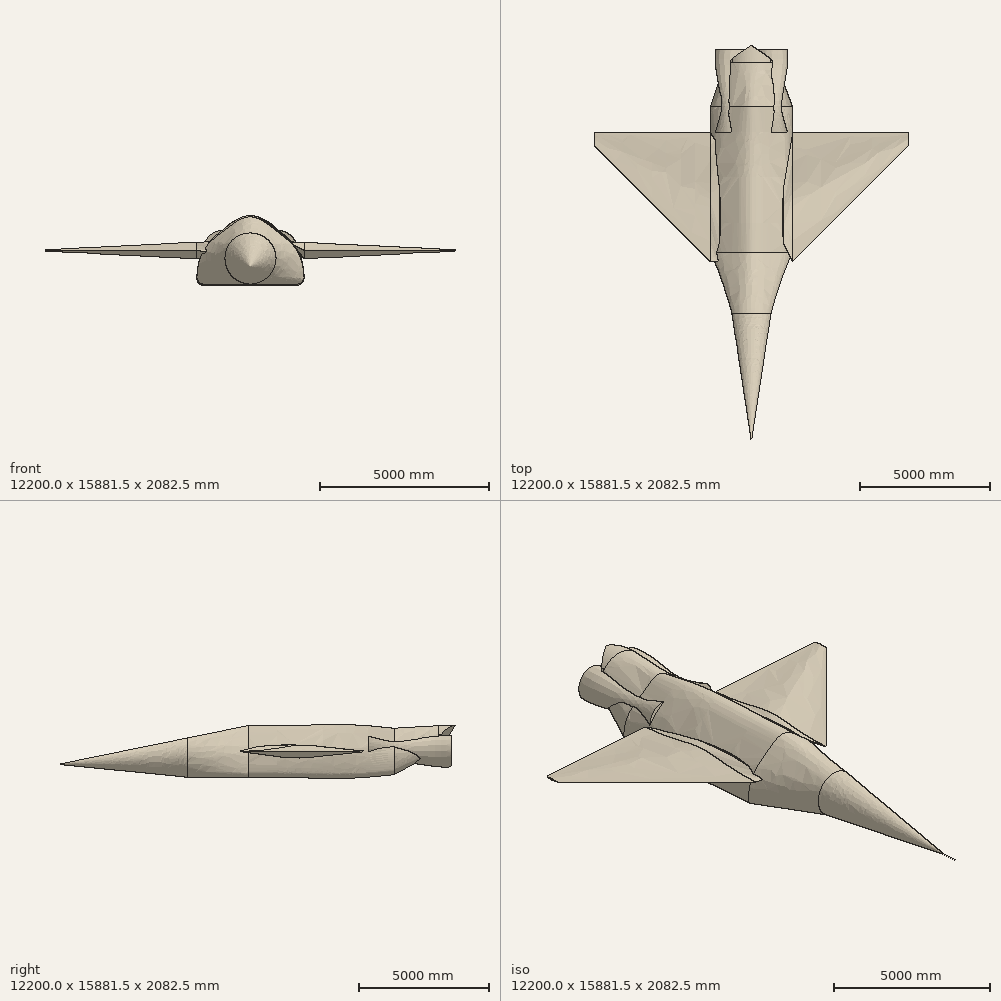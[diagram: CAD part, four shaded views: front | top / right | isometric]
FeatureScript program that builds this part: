
annotation { "Feature Type Name" : "Feature", "Feature Type Description" : "" }
export const myFeature = defineFeature(function(context is Context, id is Id, definition is map)
    precondition{}
    {
        {
            var Q0;
            Q0=qCreatedBy(makeId("Right.planeOp"),FACE);
            var sketch = newSketch(context, id + "F0", { "sketchPlane" : qUnion([Q0])});
            skLineSegment(sketch, "E0", {"start": v(0, 0) * mm, "end": v(-1750, 0) * mm});
            skLineSegment(sketch, "E1", {"start": v(-1750, 0) * mm, "end": v(-3500, 0) * mm});
            skLineSegment(sketch, "E2", {"start": v(-3500, 0) * mm, "end": v(-3500, -1000) * mm});
            skLineSegment(sketch, "E3", {"start": v(-3500, -1000) * mm, "end": v(-8500, -1000) * mm});
            skLineSegment(sketch, "E4", {"start": v(-8500, -1000) * mm, "end": v(-8500, -499.31) * mm});
            skLineSegment(sketch, "E5", {"start": v(-1151.4, 0) * mm, "end": v(-1151.4, 1000) * mm});
            skLineSegment(sketch, "E6", {"start": v(-1151.4, 1000) * mm, "end": v(-8500, -499.31) * mm});
            skLineSegment(sketch, "E7", {"start": v(-8500, -499.31) * mm, "end": v(-3500, -1000) * mm});
            skLineSegment(sketch, "E8", {"start": v(-3500, 0) * mm, "end": v(-3500, 520.82) * mm});
            skLineSegment(sketch, "E9", {"start": v(-8500, -499.31) * mm, "end": v(-8450, -499.31) * mm});
            skLineSegment(sketch, "E10", {"start": v(-8450, -499.31) * mm, "end": v(-8450, -489.1) * mm});
            skLineSegment(sketch, "E11", {"start": v(-8450, -499.31) * mm, "end": v(-8450, -504.32) * mm});
            skSolve(sketch);
        }
        {
            var Q0;
            Q0=sQuery(id+"F0.wireOp",EDGE,"E5");
            cPlane(context, id + "F1", {"entities" : qUnion([Q0]), "cplaneType" : CPlaneType.LINE_ANGLE, "offset" : 25 * mm, "angle" : 90 * degree, "oppositeDirection" : true, "width" : 150 * mm, "height" : 150 * mm});
        }
        {
            var Q0;
            Q0=qCreatedBy(id+"F1.planeOp",FACE);
            var sketch = newSketch(context, id + "F2", { "sketchPlane" : qUnion([Q0])});
            skLineSegment(sketch, "E12.top", {"start": v(-1394.2, -1000) * mm, "end": v(1394.2, -1000) * mm});
            skPoint(sketch, "E12.middle", {"position": v(0, 0) * mm});
            skFitSpline(sketch, "E13", {"points": [v(-1600, -1000) * mm, v(-848, 530) * mm, v(0, 1000) * mm, v(848, 530) * mm, v(1600, -1000) * mm], "startDerivative": vector(0, 10524.75) * mm, "endDerivative": vector(0, -10524.75) * mm});
            skArc(sketch, "E14", {"start": v(-735.27, 618.52) * mm, "mid": v(-1273.27, 435.52) * mm, "end": v(-1440.68, -107.53) * mm});
            skArc(sketch, "E15", {"start": v(1440.68, -107.53) * mm, "mid": v(1273.27, 435.52) * mm, "end": v(735.27, 618.52) * mm});
            skFitSpline(sketch, "E16.trimOffspring", {"points": [v(-1600, -1000) * mm, v(-848, 530) * mm, v(0, 1000) * mm, v(848, 530) * mm, v(1600, -1000) * mm], "startDerivative": vector(0, 10524.75) * mm, "endDerivative": vector(0, -10524.75) * mm});
            skFitSpline(sketch, "E17.trimOffspring", {"points": [v(-1600, -1000) * mm, v(-848, 530) * mm, v(0, 1000) * mm, v(848, 530) * mm, v(1600, -1000) * mm], "startDerivative": vector(0, 10524.75) * mm, "endDerivative": vector(0, -10524.75) * mm});
            skArc(sketch, "E18.filletArc", {"start": v(-1593.82, -787.83) * mm, "mid": v(-1539.85, -937.05) * mm, "end": v(-1394.2, -1000) * mm});
            skArc(sketch, "E19.filletArc", {"start": v(1394.2, -1000) * mm, "mid": v(1539.85, -937.05) * mm, "end": v(1593.82, -787.83) * mm});
            skSolve(sketch);
        }
        {
            var Q0;
            Q0=qCreatedBy(makeId("Front.planeOp"),FACE);
            var sketch = newSketch(context, id + "F3", { "sketchPlane" : qUnion([Q0])});
            skLineSegment(sketch, "E20.top", {"start": v(-1394.2, -1000) * mm, "end": v(1394.2, -1000) * mm});
            skPoint(sketch, "E20.middle", {"position": v(0, 0) * mm});
            skFitSpline(sketch, "E21", {"points": [v(-1600, -1000) * mm, v(-848, 530) * mm, v(0, 1000) * mm, v(848, 530) * mm, v(1600, -1000) * mm], "startDerivative": vector(0, 10524.75) * mm, "endDerivative": vector(0, -10524.75) * mm});
            skArc(sketch, "E22", {"start": v(-735.27, 618.52) * mm, "mid": v(-1273.27, 435.52) * mm, "end": v(-1440.68, -107.53) * mm});
            skArc(sketch, "E23", {"start": v(1440.68, -107.53) * mm, "mid": v(1273.27, 435.52) * mm, "end": v(735.27, 618.52) * mm});
            skFitSpline(sketch, "E24.trimOffspring", {"points": [v(-1600, -1000) * mm, v(-848, 530) * mm, v(0, 1000) * mm, v(848, 530) * mm, v(1600, -1000) * mm], "startDerivative": vector(0, 10524.75) * mm, "endDerivative": vector(0, -10524.75) * mm});
            skFitSpline(sketch, "E25.trimOffspring", {"points": [v(-1600, -1000) * mm, v(-848, 530) * mm, v(0, 1000) * mm, v(848, 530) * mm, v(1600, -1000) * mm], "startDerivative": vector(0, 10524.75) * mm, "endDerivative": vector(0, -10524.75) * mm});
            skArc(sketch, "E26.filletArc", {"start": v(-1593.82, -787.83) * mm, "mid": v(-1539.85, -937.05) * mm, "end": v(-1394.2, -1000) * mm});
            skArc(sketch, "E27.filletArc", {"start": v(1394.2, -1000) * mm, "mid": v(1539.85, -937.05) * mm, "end": v(1593.82, -787.83) * mm});
            skSolve(sketch);
        }
        {
            var Q0;
            Q0=qCreatedBy(makeId("Front.planeOp"),FACE);
            cPlane(context, id + "F4", {"entities" : qUnion([Q0]), "cplaneType" : CPlaneType.OFFSET, "offset" : 3500 * mm, "oppositeDirection" : true, "width" : 150 * mm, "height" : 150 * mm});
        }
        {
            var Q0;
            Q0=qCreatedBy(id+"F4.planeOp",FACE);
            var sketch = newSketch(context, id + "F5", { "sketchPlane" : qUnion([Q0])});
            skLineSegment(sketch, "E28.top", {"start": v(-1394.2, -1000) * mm, "end": v(1394.2, -1000) * mm});
            skPoint(sketch, "E28.middle", {"position": v(0, 0) * mm});
            skFitSpline(sketch, "E29", {"points": [v(-1600, -1000) * mm, v(-848, 530) * mm, v(0, 1000) * mm, v(848, 530) * mm, v(1600, -1000) * mm], "startDerivative": vector(0, 10524.75) * mm, "endDerivative": vector(0, -10524.75) * mm});
            skArc(sketch, "E30", {"start": v(-735.27, 618.52) * mm, "mid": v(-1273.27, 435.52) * mm, "end": v(-1440.68, -107.53) * mm});
            skArc(sketch, "E31", {"start": v(1440.68, -107.53) * mm, "mid": v(1273.27, 435.52) * mm, "end": v(735.27, 618.52) * mm});
            skFitSpline(sketch, "E32.trimOffspring", {"points": [v(-1600, -1000) * mm, v(-848, 530) * mm, v(0, 1000) * mm, v(848, 530) * mm, v(1600, -1000) * mm], "startDerivative": vector(0, 10524.75) * mm, "endDerivative": vector(0, -10524.75) * mm});
            skFitSpline(sketch, "E33.trimOffspring", {"points": [v(-1600, -1000) * mm, v(-848, 530) * mm, v(0, 1000) * mm, v(848, 530) * mm, v(1600, -1000) * mm], "startDerivative": vector(0, 10524.75) * mm, "endDerivative": vector(0, -10524.75) * mm});
            skArc(sketch, "E34.filletArc", {"start": v(-1593.82, -787.83) * mm, "mid": v(-1539.85, -937.05) * mm, "end": v(-1394.2, -1000) * mm});
            skArc(sketch, "E35.filletArc", {"start": v(1394.2, -1000) * mm, "mid": v(1539.85, -937.05) * mm, "end": v(1593.82, -787.83) * mm});
            skSolve(sketch);
        }
        {
            var Q0;
            Q0=qCreatedBy(makeId("Front.planeOp"),FACE);
            cPlane(context, id + "F6", {"entities" : qUnion([Q0]), "cplaneType" : CPlaneType.OFFSET, "offset" : 4500 * mm, "oppositeDirection" : true, "width" : 150 * mm, "height" : 150 * mm});
        }
        {
            var Q0;
            Q0=qCreatedBy(id+"F6.planeOp",FACE);
            var sketch = newSketch(context, id + "F7", { "sketchPlane" : qUnion([Q0])});
            skLineSegment(sketch, "E36.top", {"start": v(-1413.07, -900) * mm, "end": v(1413.07, -900) * mm});
            skPoint(sketch, "E36.middle", {"position": v(0, 0) * mm});
            skFitSpline(sketch, "E37", {"points": [v(-1600, -900) * mm, v(-784.42, 441.24) * mm, v(0, 900) * mm, v(784.42, 441.24) * mm, v(1600, -900) * mm], "startDerivative": vector(0, 9508.62) * mm, "endDerivative": vector(0, -9508.62) * mm});
            skArc(sketch, "E38", {"start": v(-719.25, 488.69) * mm, "mid": v(-1131.76, 394.84) * mm, "end": v(-1324.66, 18.33) * mm});
            skArc(sketch, "E39", {"start": v(1324.66, 18.33) * mm, "mid": v(1131.76, 394.84) * mm, "end": v(719.25, 488.69) * mm});
            skFitSpline(sketch, "E40.trimOffspring", {"points": [v(-1600, -900) * mm, v(-784.42, 441.24) * mm, v(0, 900) * mm, v(784.42, 441.24) * mm, v(1600, -900) * mm], "startDerivative": vector(0, 9508.62) * mm, "endDerivative": vector(0, -9508.62) * mm});
            skFitSpline(sketch, "E41.trimOffspring", {"points": [v(-1600, -900) * mm, v(-784.42, 441.24) * mm, v(0, 900) * mm, v(784.42, 441.24) * mm, v(1600, -900) * mm], "startDerivative": vector(0, 9508.62) * mm, "endDerivative": vector(0, -9508.62) * mm});
            skArc(sketch, "E42.filletArc", {"start": v(-1592.48, -705.43) * mm, "mid": v(-1545.4, -842.02) * mm, "end": v(-1413.07, -900) * mm});
            skArc(sketch, "E43.filletArc", {"start": v(1413.07, -900) * mm, "mid": v(1545.4, -842.02) * mm, "end": v(1592.48, -705.43) * mm});
            skLineSegment(sketch, "E44", {"start": v(-719.25, 488.69) * mm, "end": v(-1324.66, 18.33) * mm, "construction": true});
            skLineSegment(sketch, "E45", {"start": v(719.25, 488.69) * mm, "end": v(1324.66, 18.33) * mm, "construction": true});
            skSolve(sketch);
        }
        {
            var Q0;
            Q0=qCreatedBy(makeId("Front.planeOp"),FACE);
            cPlane(context, id + "F8", {"entities" : qUnion([Q0]), "cplaneType" : CPlaneType.OFFSET, "offset" : 6232.05 * mm, "oppositeDirection" : true, "width" : 150 * mm, "height" : 150 * mm});
        }
        {
            var Q0;
            Q0=qCreatedBy(id+"F8.planeOp",FACE);
            var sketch = newSketch(context, id + "F9", { "sketchPlane" : qUnion([Q0])});
            skArc(sketch, "E46", {"start": v(998.61, 52.63) * mm, "mid": v(0, 1000) * mm, "end": v(-998.61, 52.63) * mm});
            skLineSegment(sketch, "E47", {"start": v(0, 0) * mm, "end": v(-948.68, 0) * mm});
            skLineSegment(sketch, "E48", {"start": v(0, 0) * mm, "end": v(948.68, 0) * mm});
            skLineSegment(sketch, "E49", {"start": v(0, 1000) * mm, "end": v(0, 675) * mm, "construction": true});
            skLineSegment(sketch, "E50", {"start": v(0, 675) * mm, "end": v(-737.82, 675) * mm, "construction": true});
            skLineSegment(sketch, "E51", {"start": v(0, 675) * mm, "end": v(737.82, 675) * mm, "construction": true});
            skPoint(sketch, "E52.visualSharp", {"position": v(-1000, 0) * mm});
            skArc(sketch, "E52.filletArc", {"start": v(-998.61, 52.63) * mm, "mid": v(-984.96, 15.59) * mm, "end": v(-948.68, 0) * mm});
            skPoint(sketch, "E53.visualSharp", {"position": v(1000, 0) * mm});
            skArc(sketch, "E53.filletArc", {"start": v(948.68, 0) * mm, "mid": v(984.96, 15.59) * mm, "end": v(998.61, 52.63) * mm});
            skSolve(sketch);
        }
        {
            var Q0;
            Q0=makeQuery(id+"F2.imprint","IMPRINT",FACE,{"disambiguationData":[TD([[makeQuery(id+"F2.imprint","IMPRINT",EDGE,{"derivedFrom":sQuery(id+"F2.wireOp",EDGE,"E12.top")}),1.0]])]});
            var Q1;
            Q1=makeQuery(id+"F3.imprint","IMPRINT",FACE,{"disambiguationData":[TD([[makeQuery(id+"F3.imprint","IMPRINT",EDGE,{"derivedFrom":sQuery(id+"F3.wireOp",EDGE,"E20.top")}),1.0]])]});
            var Q2;
            Q2=makeQuery(id+"F5.imprint","IMPRINT",FACE,{"disambiguationData":[TD([[makeQuery(id+"F5.imprint","IMPRINT",EDGE,{"derivedFrom":sQuery(id+"F5.wireOp",EDGE,"E28.top")}),1.0]])]});
            var Q3;
            Q3=makeQuery(id+"F7.imprint","IMPRINT",FACE,{"disambiguationData":[TD([[makeQuery(id+"F7.imprint","IMPRINT",EDGE,{"derivedFrom":sQuery(id+"F7.wireOp",EDGE,"E36.top")}),1.0]])]});
            loft(context, id + "F10", {"sheetProfilesArray" : [{ "sheetProfileEntities" : qUnion([Q0]) }, { "sheetProfileEntities" : qUnion([Q1]) }, { "sheetProfileEntities" : qUnion([Q2]) }, { "sheetProfileEntities" : qUnion([Q3]) }]});
        }
        {
            var Q0;
            Q0=sQuery(id+"F7.wireOp",EDGE,"E44");
            var Q1;
            Q1=sQuery(id+"F9.wireOp",VERTEX,"E50.end");
            cPlane(context, id + "F11", {"entities" : qUnion([Q0, Q1]), "cplaneType" : CPlaneType.LINE_ANGLE, "offset" : 25 * mm, "angle" : 180 * degree, "width" : 150 * mm, "height" : 150 * mm});
        }
        {
            var Q0;
            Q0=qCreatedBy(id+"F11.planeOp",FACE);
            var sketch = newSketch(context, id + "F12", { "sketchPlane" : qUnion([Q0])});
            skLineSegment(sketch, "E54", {"start": v(-589.34, 4526.34) * mm, "end": v(-612.8, 6268.32) * mm});
            skLineSegment(sketch, "E55", {"start": v(-1354.08, 4472.19) * mm, "end": v(-612.8, 6268.32) * mm});
            skSolve(sketch);
        }
        {
            var Q0;
            Q0=sQuery(id+"F7.wireOp",EDGE,"E45");
            var Q1;
            Q1=sQuery(id+"F9.wireOp",VERTEX,"E51.end");
            cPlane(context, id + "F13", {"entities" : qUnion([Q0, Q1]), "cplaneType" : CPlaneType.LINE_ANGLE, "offset" : 25 * mm, "angle" : 0 * degree, "width" : 150 * mm, "height" : 150 * mm});
        }
        {
            var Q0;
            Q0=qCreatedBy(id+"F13.planeOp",FACE);
            var sketch = newSketch(context, id + "F14", { "sketchPlane" : qUnion([Q0])});
            skLineSegment(sketch, "E56", {"start": v(589.34, 4526.34) * mm, "end": v(612.8, 6268.32) * mm});
            skLineSegment(sketch, "E57", {"start": v(1354.08, 4472.19) * mm, "end": v(612.8, 6268.32) * mm});
            skSolve(sketch);
        }
        {
            var Q1;
            Q1=makeQuery(id+"F10.opLoft","CAP_FACE",FACE,{"disambiguationData":[OSD([makeQuery(id+"F7.imprint","IMPRINT",FACE,{"disambiguationData":[TD([[makeQuery(id+"F7.imprint","IMPRINT",EDGE,{"derivedFrom":sQuery(id+"F7.wireOp",EDGE,"E36.top")}),1.0]])]})])],"isStart":true});
            var Q2;
            Q2=makeQuery(id+"F9.imprint","IMPRINT",FACE,{"disambiguationData":[TD([[makeQuery(id+"F9.imprint","IMPRINT",EDGE,{"derivedFrom":sQuery(id+"F9.wireOp",EDGE,"E46")}),1.0]])]});
            var Q3;
            Q3=sQuery(id+"F12.wireOp",EDGE,"E54");
            var Q4;
            Q4=sQuery(id+"F14.wireOp",EDGE,"E56");
            loft(context, id + "F15", {"operationType" : NewBodyOperationType.ADD, "addGuides" : true, "sheetProfilesArray" : [{ "sheetProfileEntities" : qUnion([Q1]) }, { "sheetProfileEntities" : qUnion([Q2]) }], "guidesArray" : [{ "guideEntities" : qUnion([Q3]), "guideDerivativeType" : LoftGuideDerivativeType.DEFAULT, "guideDerivativeMagnitude" : 1 }, { "guideEntities" : qUnion([Q4]), "guideDerivativeType" : LoftGuideDerivativeType.DEFAULT, "guideDerivativeMagnitude" : 1 }]});
        }
        {
            var Q0;
            Q0=makeQuery(id+"F15.opLoft","CAP_FACE",FACE,{"disambiguationData":[OSD([makeQuery(id+"F9.imprint","IMPRINT",FACE,{"disambiguationData":[TD([[makeQuery(id+"F9.imprint","IMPRINT",EDGE,{"derivedFrom":sQuery(id+"F9.wireOp",EDGE,"E46")}),1.0]])]})])],"isStart":true});
            extrude(context, id + "F16", {"entities" : qUnion([Q0]), "operationType" : NewBodyOperationType.ADD, "depth" : 649.4 * mm, "offsetDistance" : 25 * mm});
        }
        {
            var Q0;
            Q0=qCreatedBy(makeId("Right.planeOp"),FACE);
            var sketch = newSketch(context, id + "F17", { "sketchPlane" : qUnion([Q0])});
            skLineSegment(sketch, "E58", {"start": v(0, 0) * mm, "end": v(4500, 0) * mm});
            skLineSegment(sketch, "E59", {"start": v(4500, 0) * mm, "end": v(6232.05, 0) * mm});
            skLineSegment(sketch, "E60", {"start": v(4500, 0) * mm, "end": v(4500, 1000) * mm});
            skLineSegment(sketch, "E61", {"start": v(4500, 1000) * mm, "end": v(6881.46, 1000) * mm});
            skLineSegment(sketch, "E62", {"start": v(6881.46, 1000) * mm, "end": v(6881.46, -1000) * mm});
            skLineSegment(sketch, "E63", {"start": v(6881.46, 1000) * mm, "end": v(6232.05, 0) * mm});
            skLineSegment(sketch, "E64", {"start": v(6232.05, 0) * mm, "end": v(5582.64, -1000) * mm});
            skLineSegment(sketch, "E65", {"start": v(5582.64, -1000) * mm, "end": v(6881.46, -1000) * mm});
            skSolve(sketch);
        }
        {
            var Q0;
            Q0=makeQuery(id+"F17.imprint","IMPRINT",FACE,{"disambiguationData":[TD([[makeQuery(id+"F17.imprint","IMPRINT",EDGE,{"derivedFrom":sQuery(id+"F17.wireOp",EDGE,"E62")}),-1.0]])]});
            var Q1;
            Q1=sQuery(id+"F17.wireOp",EDGE,"E61");
            revolve(context, id + "F18", {"operationType" : NewBodyOperationType.REMOVE, "entities" : qUnion([Q0]), "axis" : qUnion([Q1]), "revolveType" : RevolveType.SYMMETRIC, "oppositeDirection" : true, "angle" : 182 * degree});
        }
        {
            var Q0;
            Q0=qCreatedBy(id+"F1.planeOp",FACE);
            var sketch = newSketch(context, id + "F19", { "sketchPlane" : qUnion([Q0])});
            skLineSegment(sketch, "E66.top", {"start": v(-1394.2, -1000) * mm, "end": v(1394.2, -1000) * mm});
            skPoint(sketch, "E66.middle", {"position": v(0, 0) * mm});
            skFitSpline(sketch, "E67", {"points": [v(-1600, -1000) * mm, v(-848, 530) * mm, v(0, 1000) * mm, v(848, 530) * mm, v(1600, -1000) * mm], "startDerivative": vector(0, 10524.75) * mm, "endDerivative": vector(0, -10524.75) * mm});
            skArc(sketch, "E68.filletArc", {"start": v(-1593.82, -787.83) * mm, "mid": v(-1539.85, -937.05) * mm, "end": v(-1394.2, -1000) * mm});
            skArc(sketch, "E69.filletArc", {"start": v(1394.2, -1000) * mm, "mid": v(1539.85, -937.05) * mm, "end": v(1593.82, -787.83) * mm});
            skLineSegment(sketch, "E70", {"start": v(-1593.82, -787.83) * mm, "end": v(-1394.2, -1000) * mm, "construction": true});
            skLineSegment(sketch, "E71", {"start": v(1593.82, -787.83) * mm, "end": v(1394.2, -1000) * mm, "construction": true});
            skSolve(sketch);
        }
        {
            var Q0;
            Q0=qCreatedBy(makeId("Front.planeOp"),FACE);
            cPlane(context, id + "F20", {"entities" : qUnion([Q0]), "cplaneType" : CPlaneType.OFFSET, "offset" : 3500 * mm, "width" : 150 * mm, "height" : 150 * mm});
        }
        {
            var Q0;
            Q0=qCreatedBy(id+"F20.planeOp",FACE);
            var sketch = newSketch(context, id + "F21", { "sketchPlane" : qUnion([Q0])});
            skCircle(sketch, "E72", {"center": v(0, -239.59) * mm, "radius": 760.41 * mm});
            skLineSegment(sketch, "E73", {"start": v(0, -1000) * mm, "end": v(0, -800) * mm, "construction": true});
            skLineSegment(sketch, "E74", {"start": v(0, -800) * mm, "end": v(-513.97, -800) * mm, "construction": true});
            skLineSegment(sketch, "E75", {"start": v(0, -800) * mm, "end": v(513.97, -800) * mm, "construction": true});
            skSolve(sketch);
        }
        {
            var Q0;
            Q0=qCreatedBy(makeId("Front.planeOp"),FACE);
            cPlane(context, id + "F22", {"entities" : qUnion([Q0]), "cplaneType" : CPlaneType.OFFSET, "offset" : 8450 * mm, "width" : 150 * mm, "height" : 150 * mm});
        }
        {
            var Q0;
            Q0=qCreatedBy(id+"F22.planeOp",FACE);
            var sketch = newSketch(context, id + "F23", { "sketchPlane" : qUnion([Q0])});
            skCircle(sketch, "E76", {"center": v(0, -496.71) * mm, "radius": 7.6 * mm});
            skSolve(sketch);
        }
        {
            var Q0;
            Q0=sQuery(id+"F19.wireOp",EDGE,"E70");
            var Q1;
            Q1=sQuery(id+"F21.wireOp",VERTEX,"E74.end");
            cPlane(context, id + "F24", {"entities" : qUnion([Q0, Q1]), "cplaneType" : CPlaneType.LINE_ANGLE, "offset" : 25 * mm, "angle" : 0 * degree, "width" : 150 * mm, "height" : 150 * mm});
        }
        {
            var Q0;
            Q0=qCreatedBy(id+"F24.planeOp",FACE);
            var sketch = newSketch(context, id + "F25", { "sketchPlane" : qUnion([Q0])});
            skLineSegment(sketch, "E77", {"start": v(3032.27, -230.44) * mm, "end": v(558.11, 518.4) * mm});
            skLineSegment(sketch, "E78", {"start": v(3032.27, -230.44) * mm, "end": v(558.11, 227.09) * mm});
            skSolve(sketch);
        }
        {
            var Q0;
            Q0=sQuery(id+"F19.wireOp",EDGE,"E71");
            var Q1;
            Q1=sQuery(id+"F21.wireOp",VERTEX,"E75.end");
            cPlane(context, id + "F26", {"entities" : qUnion([Q0, Q1]), "cplaneType" : CPlaneType.LINE_ANGLE, "offset" : 25 * mm, "angle" : 180 * degree, "width" : 150 * mm, "height" : 150 * mm});
        }
        {
            var Q0;
            Q0=qCreatedBy(id+"F26.planeOp",FACE);
            var sketch = newSketch(context, id + "F27", { "sketchPlane" : qUnion([Q0])});
            skLineSegment(sketch, "E79", {"start": v(-3032.27, -230.44) * mm, "end": v(-558.11, 518.4) * mm});
            skLineSegment(sketch, "E80", {"start": v(-3032.27, -230.44) * mm, "end": v(-558.11, 227.09) * mm});
            skSolve(sketch);
        }
        {
            var Q1;
            Q1=makeQuery(id+"F19.imprint","IMPRINT",FACE,{"disambiguationData":[TD([[makeQuery(id+"F19.imprint","IMPRINT",EDGE,{"derivedFrom":sQuery(id+"F19.wireOp",EDGE,"E66.top")}),1.0]])]});
            var Q2;
            Q2=makeQuery(id+"F21.imprint","IMPRINT",FACE,{"disambiguationData":[TD([[makeQuery(id+"F21.imprint","IMPRINT",EDGE,{"derivedFrom":sQuery(id+"F21.wireOp",EDGE,"E72")}),1.0]])]});
            var Q3;
            Q3=sQuery(id+"F25.wireOp",EDGE,"E77");
            var Q4;
            Q4=sQuery(id+"F27.wireOp",EDGE,"E79");
            loft(context, id + "F28", {"operationType" : NewBodyOperationType.ADD, "addGuides" : true, "sheetProfilesArray" : [{ "sheetProfileEntities" : qUnion([Q1]) }, { "sheetProfileEntities" : qUnion([Q2]) }], "guidesArray" : [{ "guideEntities" : qUnion([Q3]), "guideDerivativeType" : LoftGuideDerivativeType.DEFAULT, "guideDerivativeMagnitude" : 1 }, { "guideEntities" : qUnion([Q4]), "guideDerivativeType" : LoftGuideDerivativeType.DEFAULT, "guideDerivativeMagnitude" : 1 }]});
        }
        {
            var Q1;
            Q1=makeQuery(id+"F28.opLoft","CAP_FACE",FACE,{"disambiguationData":[OSD([makeQuery(id+"F21.imprint","IMPRINT",FACE,{"disambiguationData":[TD([[makeQuery(id+"F21.imprint","IMPRINT",EDGE,{"derivedFrom":sQuery(id+"F21.wireOp",EDGE,"E72")}),1.0]])]})])],"isStart":true});
            var Q2;
            Q2=makeQuery(id+"F23.imprint","IMPRINT",FACE,{"disambiguationData":[TD([[makeQuery(id+"F23.imprint","IMPRINT",EDGE,{"derivedFrom":sQuery(id+"F23.wireOp",EDGE,"E76")}),1.0]])]});
            loft(context, id + "F29", {"operationType" : NewBodyOperationType.ADD, "sheetProfilesArray" : [{ "sheetProfileEntities" : qUnion([Q1]) }, { "sheetProfileEntities" : qUnion([Q2]) }]});
        }
        {
            var Q0;
            Q0=makeQuery(id+"F29.opLoft","CAP_FACE",FACE,{"disambiguationData":[OSD([makeQuery(id+"F23.imprint","IMPRINT",FACE,{"disambiguationData":[TD([[makeQuery(id+"F23.imprint","IMPRINT",EDGE,{"derivedFrom":sQuery(id+"F23.wireOp",EDGE,"E76")}),1.0]])]})])],"isStart":true});
            extrude(context, id + "F30", {"entities" : qUnion([Q0]), "operationType" : NewBodyOperationType.ADD, "depth" : 550 * mm, "offsetDistance" : 25 * mm});
        }
        {
            var Q0;
            Q0=qCreatedBy(makeId("Front.planeOp"),FACE);
            cPlane(context, id + "F31", {"entities" : qUnion([Q0]), "cplaneType" : CPlaneType.OFFSET, "offset" : 3500 * mm, "oppositeDirection" : true, "width" : 150 * mm, "height" : 150 * mm});
        }
        {
            var Q0;
            Q0=qCreatedBy(id+"F31.planeOp",FACE);
            var sketch = newSketch(context, id + "F32", { "sketchPlane" : qUnion([Q0])});
            skCircle(sketch, "E81", {"center": v(-800, 0) * mm, "radius": 600 * mm});
            skCircle(sketch, "E82", {"center": v(800, 0) * mm, "radius": 600 * mm});
            skSolve(sketch);
        }
        {
            var Q0;
            Q0=qCreatedBy(makeId("Front.planeOp"),FACE);
            cPlane(context, id + "F33", {"entities" : qUnion([Q0]), "cplaneType" : CPlaneType.OFFSET, "offset" : 4500 * mm, "oppositeDirection" : true, "width" : 150 * mm, "height" : 150 * mm});
        }
        {
            var Q0;
            Q0=qCreatedBy(id+"F33.planeOp",FACE);
            var sketch = newSketch(context, id + "F34", { "sketchPlane" : qUnion([Q0])});
            skCircle(sketch, "E83", {"center": v(-800, 0) * mm, "radius": 400 * mm});
            skCircle(sketch, "E84", {"center": v(800, 0) * mm, "radius": 400 * mm});
            skSolve(sketch);
        }
        {
            var Q0;
            Q0=qCreatedBy(makeId("Front.planeOp"),FACE);
            cPlane(context, id + "F35", {"entities" : qUnion([Q0]), "cplaneType" : CPlaneType.OFFSET, "offset" : 6232.05 * mm, "oppositeDirection" : true, "width" : 150 * mm, "height" : 150 * mm});
        }
        {
            var Q0;
            Q0=qCreatedBy(id+"F35.planeOp",FACE);
            var sketch = newSketch(context, id + "F36", { "sketchPlane" : qUnion([Q0])});
            skCircle(sketch, "E85", {"center": v(-800, 0) * mm, "radius": 600 * mm});
            skCircle(sketch, "E86", {"center": v(800, 0) * mm, "radius": 600 * mm});
            skSolve(sketch);
        }
        {
            var Q0;
            Q0=qCreatedBy(makeId("Front.planeOp"),FACE);
            cPlane(context, id + "F37", {"entities" : qUnion([Q0]), "cplaneType" : CPlaneType.OFFSET, "offset" : 6732.05 * mm, "oppositeDirection" : true, "width" : 150 * mm, "height" : 150 * mm});
        }
        {
            var Q0;
            Q0=qCreatedBy(id+"F37.planeOp",FACE);
            var sketch = newSketch(context, id + "F38", { "sketchPlane" : qUnion([Q0])});
            skCircle(sketch, "E87", {"center": v(-800, 0) * mm, "radius": 600 * mm});
            skCircle(sketch, "E88", {"center": v(800, 0) * mm, "radius": 600 * mm});
            skSolve(sketch);
        }
        {
            var Q0;
            Q0=makeQuery(id+"F32.imprint","IMPRINT",FACE,{"disambiguationData":[TD([[makeQuery(id+"F32.imprint","IMPRINT",EDGE,{"derivedFrom":sQuery(id+"F32.wireOp",EDGE,"E81")}),1.0]])]});
            var Q1;
            Q1=makeQuery(id+"F34.imprint","IMPRINT",FACE,{"disambiguationData":[TD([[makeQuery(id+"F34.imprint","IMPRINT",EDGE,{"derivedFrom":sQuery(id+"F34.wireOp",EDGE,"E83")}),1.0]])]});
            var Q2;
            Q2=makeQuery(id+"F36.imprint","IMPRINT",FACE,{"disambiguationData":[TD([[makeQuery(id+"F36.imprint","IMPRINT",EDGE,{"derivedFrom":sQuery(id+"F36.wireOp",EDGE,"E85")}),1.0]])]});
            var Q3;
            Q3=makeQuery(id+"F38.imprint","IMPRINT",FACE,{"disambiguationData":[TD([[makeQuery(id+"F38.imprint","IMPRINT",EDGE,{"derivedFrom":sQuery(id+"F38.wireOp",EDGE,"E87")}),1.0]])]});
            loft(context, id + "F39", {"sheetProfilesArray" : [{ "sheetProfileEntities" : qUnion([Q0]) }, { "sheetProfileEntities" : qUnion([Q1]) }, { "sheetProfileEntities" : qUnion([Q2]) }, { "sheetProfileEntities" : qUnion([Q3]) }]});
        }
        {
            var Q0;
            Q0=makeQuery(id+"F32.imprint","IMPRINT",FACE,{"disambiguationData":[TD([[makeQuery(id+"F32.imprint","IMPRINT",EDGE,{"derivedFrom":sQuery(id+"F32.wireOp",EDGE,"E82")}),1.0]])]});
            var Q1;
            Q1=makeQuery(id+"F34.imprint","IMPRINT",FACE,{"disambiguationData":[TD([[makeQuery(id+"F34.imprint","IMPRINT",EDGE,{"derivedFrom":sQuery(id+"F34.wireOp",EDGE,"E84")}),1.0]])]});
            var Q2;
            Q2=makeQuery(id+"F36.imprint","IMPRINT",FACE,{"disambiguationData":[TD([[makeQuery(id+"F36.imprint","IMPRINT",EDGE,{"derivedFrom":sQuery(id+"F36.wireOp",EDGE,"E86")}),1.0]])]});
            var Q3;
            Q3=makeQuery(id+"F38.imprint","IMPRINT",FACE,{"disambiguationData":[TD([[makeQuery(id+"F38.imprint","IMPRINT",EDGE,{"derivedFrom":sQuery(id+"F38.wireOp",EDGE,"E88")}),1.0]])]});
            loft(context, id + "F40", {"sheetProfilesArray" : [{ "sheetProfileEntities" : qUnion([Q0]) }, { "sheetProfileEntities" : qUnion([Q1]) }, { "sheetProfileEntities" : qUnion([Q2]) }, { "sheetProfileEntities" : qUnion([Q3]) }]});
        }
        {
            var Q0;
            Q0=qCreatedBy(makeId("Right.planeOp"),FACE);
            var sketch = newSketch(context, id + "F41", { "sketchPlane" : qUnion([Q0])});
            skFitSpline(sketch, "E89", {"points": [v(-1500, -50) * mm, v(0, 250) * mm, v(3000, -50) * mm, v(0, -250) * mm, v(-1500, -50) * mm]});
            skSolve(sketch);
        }
        {
            var Q0;
            Q0=qCreatedBy(makeId("Right.planeOp"),FACE);
            cPlane(context, id + "F42", {"entities" : qUnion([Q0]), "cplaneType" : CPlaneType.OFFSET, "offset" : 1600 * mm, "oppositeDirection" : true, "width" : 150 * mm, "height" : 150 * mm});
        }
        {
            var Q0;
            Q0=qCreatedBy(id+"F42.planeOp",FACE);
            var sketch = newSketch(context, id + "F43", { "sketchPlane" : qUnion([Q0])});
            skFitSpline(sketch, "E90", {"points": [v(-1500, 0) * mm, v(1000, 250) * mm, v(3500, 0) * mm], "startDerivative": vector(7500, 0) * mm, "endDerivative": vector(7500, 0) * mm});
            skFitSpline(sketch, "E91", {"points": [v(-1500, 0) * mm, v(1000, -250) * mm, v(3500, 0) * mm], "startDerivative": vector(5000, -750) * mm, "endDerivative": vector(7500, 0) * mm});
            skSolve(sketch);
        }
        {
            var Q0;
            Q0=qCreatedBy(makeId("Right.planeOp"),FACE);
            cPlane(context, id + "F44", {"entities" : qUnion([Q0]), "cplaneType" : CPlaneType.OFFSET, "offset" : 1600 * mm, "width" : 150 * mm, "height" : 150 * mm});
        }
        {
            var Q0;
            Q0=qCreatedBy(id+"F44.planeOp",FACE);
            var sketch = newSketch(context, id + "F45", { "sketchPlane" : qUnion([Q0])});
            skFitSpline(sketch, "E92", {"points": [v(-1500, 0) * mm, v(1000, 250) * mm, v(3500, 0) * mm], "startDerivative": vector(7500, 0) * mm, "endDerivative": vector(7500, 0) * mm});
            skFitSpline(sketch, "E93", {"points": [v(-1500, 0) * mm, v(1000, -250) * mm, v(3500, 0) * mm], "startDerivative": vector(5000, -750) * mm, "endDerivative": vector(7500, 0) * mm});
            skSolve(sketch);
        }
        {
            var Q0;
            Q0=qCreatedBy(makeId("Right.planeOp"),FACE);
            cPlane(context, id + "F46", {"entities" : qUnion([Q0]), "cplaneType" : CPlaneType.OFFSET, "offset" : 6100 * mm, "oppositeDirection" : true, "width" : 150 * mm, "height" : 150 * mm});
        }
        {
            var Q0;
            Q0=qCreatedBy(id+"F46.planeOp",FACE);
            var sketch = newSketch(context, id + "F47", { "sketchPlane" : qUnion([Q0])});
            skFitSpline(sketch, "E94", {"points": [v(3000, 0) * mm, v(3250, 25) * mm, v(3500, 0) * mm], "startDerivative": vector(750, 0) * mm, "endDerivative": vector(750, 0) * mm});
            skFitSpline(sketch, "E95", {"points": [v(3000, 0) * mm, v(3250, -25) * mm, v(3500, 0) * mm], "startDerivative": vector(500, -75) * mm, "endDerivative": vector(750, 0) * mm});
            skSolve(sketch);
        }
        {
            var Q0;
            Q0=qCreatedBy(makeId("Right.planeOp"),FACE);
            cPlane(context, id + "F48", {"entities" : qUnion([Q0]), "cplaneType" : CPlaneType.OFFSET, "offset" : 6100 * mm, "width" : 150 * mm, "height" : 150 * mm});
        }
        {
            var Q0;
            Q0=qCreatedBy(id+"F48.planeOp",FACE);
            var sketch = newSketch(context, id + "F49", { "sketchPlane" : qUnion([Q0])});
            skFitSpline(sketch, "E96", {"points": [v(3000, 0) * mm, v(3250, 25) * mm, v(3500, 0) * mm], "startDerivative": vector(750, 0) * mm, "endDerivative": vector(750, 0) * mm});
            skFitSpline(sketch, "E97", {"points": [v(3000, 0) * mm, v(3250, -25) * mm, v(3500, 0) * mm], "startDerivative": vector(500, -75) * mm, "endDerivative": vector(750, 0) * mm});
            skSolve(sketch);
        }
        {
            var Q0;
            Q0=qSketchRegion(id+"F41",true);
            extrude(context, id + "F50", {"entities" : qUnion([Q0]), "endBound" : BoundingType.SYMMETRIC, "depth" : 2500 * mm, "offsetDistance" : 25 * mm});
        }
        {
            var Q1;
            Q1=makeQuery(id+"F50.opExtrude","CAP_FACE",FACE,{"disambiguationData":[OSD([sQuery(id+"F41.wireOp",EDGE,"E89")])],"isStart":true});
            var Q2;
            {var subQ0=sQuery(id+"F43.wireOp",EDGE,"E90");Q2=makeQuery(id+"F43.imprint","IMPRINT",FACE,{"disambiguationData":[TD([[makeQuery(id+"F43.imprint","IMPRINT",EDGE,{"derivedFrom":subQ0}),-1.0]])]});}
            loft(context, id + "F51", {"operationType" : NewBodyOperationType.ADD, "sheetProfilesArray" : [{ "sheetProfileEntities" : qUnion([Q1]) }, { "sheetProfileEntities" : qUnion([Q2]) }]});
        }
        {
            var Q1;
            Q1=makeQuery(id+"F50.opExtrude","CAP_FACE",FACE,{"disambiguationData":[OSD([sQuery(id+"F41.wireOp",EDGE,"E89")])],"isStart":false});
            var Q2;
            {var subQ0=sQuery(id+"F45.wireOp",EDGE,"E92");Q2=makeQuery(id+"F45.imprint","IMPRINT",FACE,{"disambiguationData":[TD([[makeQuery(id+"F45.imprint","IMPRINT",EDGE,{"derivedFrom":subQ0}),-1.0]])]});}
            loft(context, id + "F52", {"operationType" : NewBodyOperationType.ADD, "sheetProfilesArray" : [{ "sheetProfileEntities" : qUnion([Q1]) }, { "sheetProfileEntities" : qUnion([Q2]) }]});
        }
        {
            var Q1;
            {var subQ0=sQuery(id+"F43.wireOp",EDGE,"E90");Q1=makeQuery(id+"F51.opLoft","CAP_FACE",FACE,{"disambiguationData":[OSD([makeQuery(id+"F43.imprint","IMPRINT",FACE,{"disambiguationData":[TD([[makeQuery(id+"F43.imprint","IMPRINT",EDGE,{"derivedFrom":subQ0}),-1.0]])]})])],"isStart":true});}
            var Q2;
            {var subQ0=sQuery(id+"F47.wireOp",EDGE,"E94");Q2=makeQuery(id+"F47.imprint","IMPRINT",FACE,{"disambiguationData":[TD([[makeQuery(id+"F47.imprint","IMPRINT",EDGE,{"derivedFrom":subQ0}),-1.0]])]});}
            loft(context, id + "F53", {"operationType" : NewBodyOperationType.ADD, "sheetProfilesArray" : [{ "sheetProfileEntities" : qUnion([Q1]) }, { "sheetProfileEntities" : qUnion([Q2]) }]});
        }
        {
            var Q1;
            {var subQ0=sQuery(id+"F45.wireOp",EDGE,"E92");Q1=makeQuery(id+"F52.opLoft","CAP_FACE",FACE,{"disambiguationData":[OSD([makeQuery(id+"F45.imprint","IMPRINT",FACE,{"disambiguationData":[TD([[makeQuery(id+"F45.imprint","IMPRINT",EDGE,{"derivedFrom":subQ0}),-1.0]])]})])],"isStart":true});}
            var Q2;
            {var subQ0=sQuery(id+"F49.wireOp",EDGE,"E96");Q2=makeQuery(id+"F49.imprint","IMPRINT",FACE,{"disambiguationData":[TD([[makeQuery(id+"F49.imprint","IMPRINT",EDGE,{"derivedFrom":subQ0}),-1.0]])]});}
            loft(context, id + "F54", {"operationType" : NewBodyOperationType.ADD, "sheetProfilesArray" : [{ "sheetProfileEntities" : qUnion([Q1]) }, { "sheetProfileEntities" : qUnion([Q2]) }]});
        }
    });
